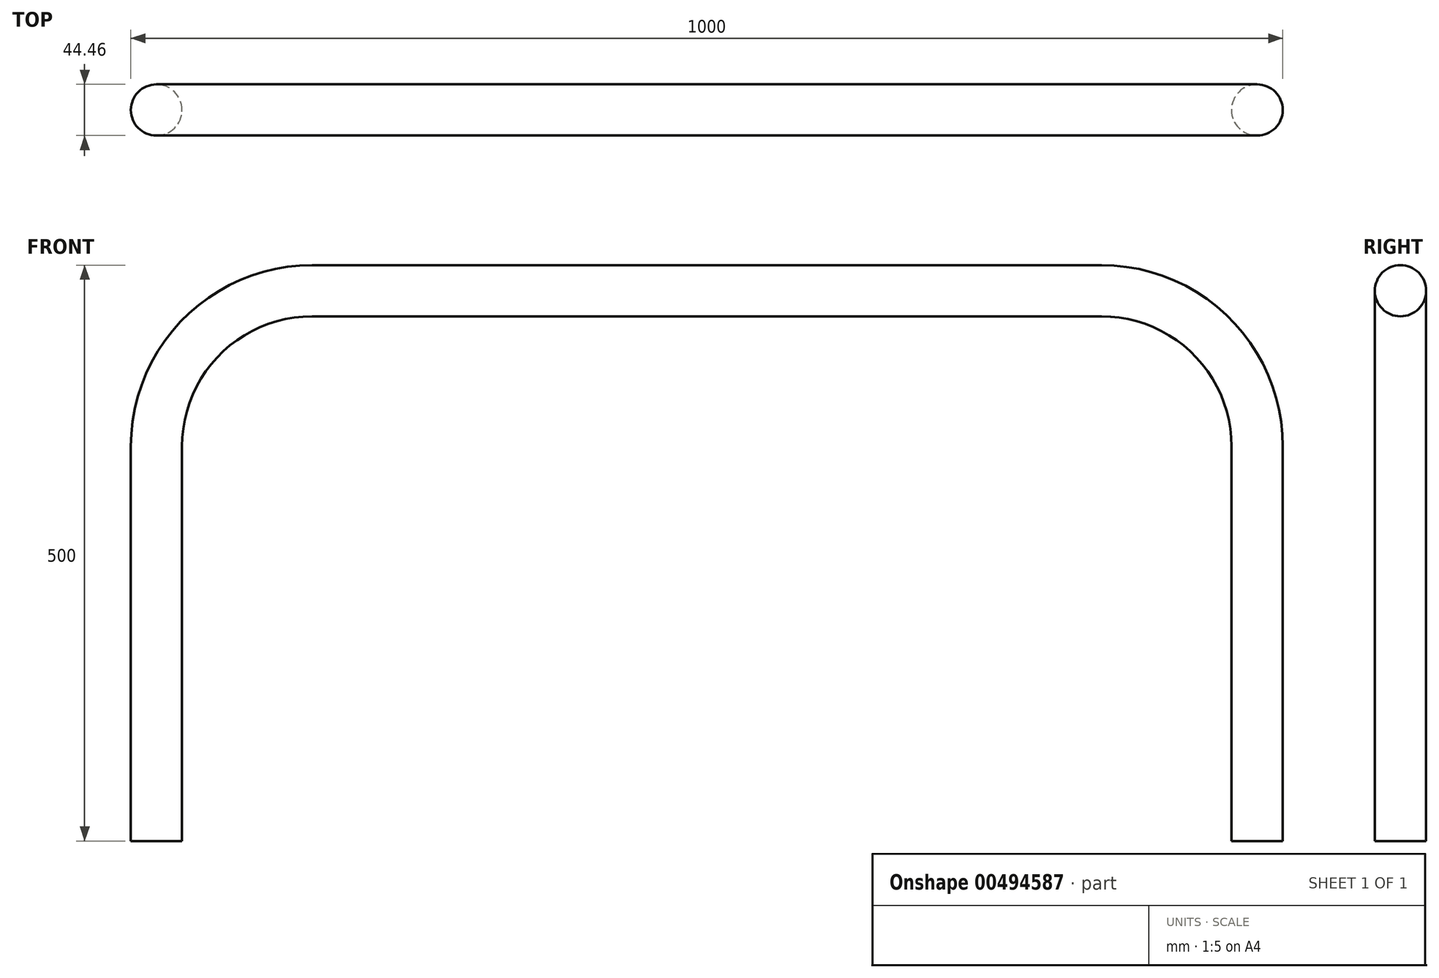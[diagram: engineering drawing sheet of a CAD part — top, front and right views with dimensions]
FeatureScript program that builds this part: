
annotation { "Feature Type Name" : "Feature", "Feature Type Description" : "" }
export const myFeature = defineFeature(function(context is Context, id is Id, definition is map)
    precondition{}
    {
        {
            var Q0;
            Q0=qCreatedBy(makeId("Front.planeOp"),FACE);
            var sketch = newSketch(context, id + "F0", { "sketchPlane" : qUnion([Q0])});
            skLineSegment(sketch, "E0", {"start": v(-477.77, 0) * mm, "end": v(-477.77, 342.77) * mm});
            skLineSegment(sketch, "E1", {"start": v(-342.78, 477.78) * mm, "end": v(342.77, 477.78) * mm});
            skLineSegment(sketch, "E2", {"start": v(477.78, 342.78) * mm, "end": v(477.78, 0) * mm});
            skPoint(sketch, "E3", {"position": v(0, 477.78) * mm});
            skPoint(sketch, "E4.visualSharp", {"position": v(-477.77, 477.77) * mm});
            skArc(sketch, "E4.filletArc", {"start": v(-342.78, 477.77) * mm, "mid": v(-438.23, 438.23) * mm, "end": v(-477.77, 342.77) * mm});
            skPoint(sketch, "E5.visualSharp", {"position": v(477.77, 477.77) * mm});
            skArc(sketch, "E5.filletArc", {"start": v(477.78, 342.78) * mm, "mid": v(438.23, 438.23) * mm, "end": v(342.77, 477.78) * mm});
            skPoint(sketch, "E6", {"position": v(477.78, 75) * mm});
            skPoint(sketch, "E7", {"position": v(-438.23, 438.23) * mm});
            skLineSegment(sketch, "E8", {"start": v(-438.23, 438.23) * mm, "end": v(477.78, 75) * mm});
            skSolve(sketch);
        }
        {
            var Q0;
            Q0=qCreatedBy(makeId("Top.planeOp"),FACE);
            var sketch = newSketch(context, id + "F1", { "sketchPlane" : qUnion([Q0])});
            skPoint(sketch, "E9.0", {"position": v(-477.77, 0) * mm});
            skCircle(sketch, "E10", {"center": v(-477.77, 0) * mm, "radius": 22.23 * mm});
            skSolve(sketch);
        }
        {
            var Q0;
            Q0=makeQuery(id+"F1.imprint","IMPRINT",FACE,{"disambiguationData":[TD([[makeQuery(id+"F1.imprint","IMPRINT",EDGE,{"derivedFrom":sQuery(id+"F1.wireOp",EDGE,"E10")}),1.0]])]});
            var Q1;
            Q1=sQuery(id+"F0.wireOp",EDGE,"E0");
            var Q2;
            Q2=sQuery(id+"F0.wireOp",EDGE,"E4.filletArc");
            var Q3;
            Q3=sQuery(id+"F0.wireOp",EDGE,"E1");
            var Q4;
            Q4=sQuery(id+"F0.wireOp",EDGE,"E5.filletArc");
            var Q5;
            Q5=sQuery(id+"F0.wireOp",EDGE,"E2");
            sweep(context, id + "F2", {"profiles" : qUnion([Q0]), "path" : qUnion([Q1, Q2, Q3, Q4, Q5])});
        }
    });
